# Revit family: EL_Marut_L
name_source: partatom
category: Lighting Fixtures
units: mm (PartAtom-declared; Revit-internal decimal feet)

## family parameters
Always vertical = Yes
Cut with Voids When Loaded = No
Light Source = Yes
Maintain Annotation Orientation = No
OmniClass Number = 23.80.70.00
OmniClass Title = Lighting
Part Type = Normal
Room Calculation Point = No
Round Connector Dimension = Use Diameter
Shared = No
Work Plane-Based = No

## types (39) — shared parameters
CE Conformity = CE Mark
Certification = ENEC, ENEC+, EMC, Zhaga D4i, IDA
Color Filter = 16777215
Control Gear = LED Driver
Default Elevation = 1500 mm
Description = Street luminaire
Diffuser Material  = Flat glass
Dimming Lamp Color Temperature Shift = <None>
EL_Voltage = AC 220V - 240V / 50-60Hz
Housing Height = 118 mm
Housing Length = 665 mm
Housing Width = 381 mm  [stored 1.25 ft]
IK = IK 09 / IK10
IP = IP66
Lamp = LED
Life Time = 120 000 h
Light Source Symbol Length = 3048 mm  [stored 10 ft]
Luminaire Material = Kov
Luminaire Type = MARUT L G2
Manufacturer = ELEKTRO-LUMEN, s. r. o.
Model = MARUT L G2
Spot Beam Angle = 30.00°
Spot Field Angle = 90.00°
Terminal Block Poles = 2, 3, 5
Tilt Angle = 90.00°
URL Luminaire = https://www.el-lumen.cz
URL Manufacturer = https://www.el-lumen.cz
Voltage  = AC 220V - 240V / 50-60Hz
Weight = 9.6

## per-type parameters (varying)
| type | CCT | CRI | Luminous Flux of LED | Luminous Flux of Luminaire | Optic | Optical Efficacy | Power |
| MARUT L G2 Mxx 18k0 740 | 4000 | 70 | 18000 lm | 15604 lm | M03 | 86.69 | 108 W |
| MARUT L G2 Mxx 16k0 740 | 4000 | 70 | 16000 lm | 13870 lm | M03 | 86.69 | 94 W |
| MARUT L G2 Mxx 15k0 740 | 4000 | 70 | 15000 lm | 13004 lm | M03 | 86.69 | 87 W |
| MARUT L G2 Mxx 14k0 740 | 4000 | 70 | 14000 lm | 12137 lm | M03 | 86.69 | 81 W |
| MARUT L G2 Mxx 12k0 740 | 4000 | 70 | 12000 lm | 10403 lm | M03 | 86.69 | 67 W |
| MARUT L G2 Mxx 10k0 740 | 4000 | 70 | 10000 lm | 8669 lm | M03 | 86.69 | 59 W |
| MARUT L G2 Mxx 9k0 740 | 4000 | 70 | 9000 lm | 7802 lm | M03 | 86.69 | 52 W |
| MARUT L G2 Mxx 8k0 740 | 4000 | 70 | 8000 lm | 6935 lm | M03 | 86.69 | 45 W |
| MARUT L G2 Mxx 7k0 740 | 4000 | 70 | 7000 lm | 6068 lm | M03 | 86.69 | 39 W |
| MARUT L G2 Mxx 16k0 730 | 3000 | 70 | 16000 lm | 13870 lm | M03 | 86.69 | 100 W |
| MARUT L G2 Mxx 15k0 730 | 3000 | 70 | 15000 lm | 13004 lm | M03 | 86.69 | 93 W |
| MARUT L G2 Mxx 14k0 730 | 3000 | 70 | 14000 lm | 12137 lm | M03 | 86.69 | 86 W |
| MARUT L G2 Mxx 12k0 730 | 3000 | 70 | 12000 lm | 10403 lm | M03 | 86.69 | 71 W |
| MARUT L G2 Mxx 10k0 730 | 3000 | 70 | 10000 lm | 8669 lm | M03 | 86.69 | 63 W |
| MARUT L G2 Mxx 9k0 730 | 3000 | 70 | 9000 lm | 7802 lm | M03 | 86.69 | 55 W |
| MARUT L G2 Mxx 8k0 730 | 3000 | 70 | 8000 lm | 6935 lm | M03 | 86.69 | 48 W |
| MARUT L G2 Mxx 7k0 730 | 3000 | 70 | 7000 lm | 6068 lm | M03 | 86.69 | 42 W |
| MARUT L G2 Mxx 16k0 727 | 2700 | 70 | 16000 lm | 13870 lm | M03 | 86.69 | 107 W |
| MARUT L G2 Mxx 15k0 727 | 2700 | 70 | 15000 lm | 13004 lm | M03 | 86.69 | 99 W |
| MARUT L G2 Mxx 14k0 727 | 2700 | 70 | 14000 lm | 12137 lm | M03 | 86.69 | 91 W |
| MARUT L G2 Mxx 12k0 727 | 2700 | 70 | 12000 lm | 10403 lm | M03 | 86.69 | 76 W |
| MARUT L G2 Mxx 10k0 727 | 2700 | 70 | 10000 lm | 8669 lm | M03 | 86.69 | 67 W |
| MARUT L G2 Mxx 9k0 727 | 2700 | 70 | 9000 lm | 7802 lm | M03 | 86.69 | 59 W |
| MARUT L G2 Mxx 8k0 727 | 2700 | 70 | 8000 lm | 6935 lm | M03 | 86.69 | 51 W |
| MARUT L G2 Mxx 7k0 727 | 2700 | 70 | 7000 lm | 6068 lm | M03 | 86.69 | 44 W |
| MARUT L G2 Mxx 14k0 722 | 2200 | 70 | 14000 lm | 12137 lm | M03 | 86.69 | 106 W |
| MARUT L G2 Mxx 12k0 722 | 2200 | 70 | 12000 lm | 10403 lm | M03 | 86.69 | 88 W |
| MARUT L G2 Mxx 10k0 722 | 2200 | 70 | 10000 lm | 8669 lm | M03 | 86.69 | 71 W |
| MARUT L G2 Mxx 9k0 722 | 2200 | 70 | 9000 lm | 7802 lm | M03 | 86.69 | 68 W |
| MARUT L G2 Mxx 8k0 722 | 2200 | 70 | 8000 lm | 6935 lm | M03 | 86.69 | 60 W |
| MARUT L G2 Mxx 7k0 722 | 2200 | 70 | 7000 lm | 6068 lm | M03 | 86.69 | 51 W |
| MARUT L G2 Lxx 16k0 AMB | 1850 | 50 | 16000 lm | 14451 lm | L03 | 90.32 | 111 W |
| MARUT L G2 Lxx 15k0 AMB | 1850 | 50 | 15000 lm | 13548 lm | L03 | 90.32 | 105 W |
| MARUT L G2 Lxx 14k0 AMB | 1850 | 50 | 14000 lm | 12645 lm | L03 | 90.32 | 97 W |
| MARUT L G2 Lxx 12k0 AMB | 1850 | 50 | 12000 lm | 10838 lm | L03 | 90.32 | 81 W |
| MARUT L G2 Lxx 10k0 AMB | 1850 | 50 | 10000 lm | 9032 lm | L03 | 90.32 | 66 W |
| MARUT L G2 Lxx 9k0 AMB | 1850 | 50 | 9000 lm | 8129 lm | L03 | 90.32 | 62 W |
| MARUT L G2 Lxx 8k0 AMB | 1850 | 50 | 8000 lm | 7226 lm | L03 | 90.32 | 54 W |
| MARUT L G2 Lxx 7k0 AMB | 1850 | 50 | 7000 lm | 6322 lm | L03 | 90.32 | 47 W |

note: column(s) folded — value = type name in every type: Luminaire Model

note: [stored X ft] marks values corroborated as IEEE doubles in the binary element streams (Revit-internal decimal feet)
